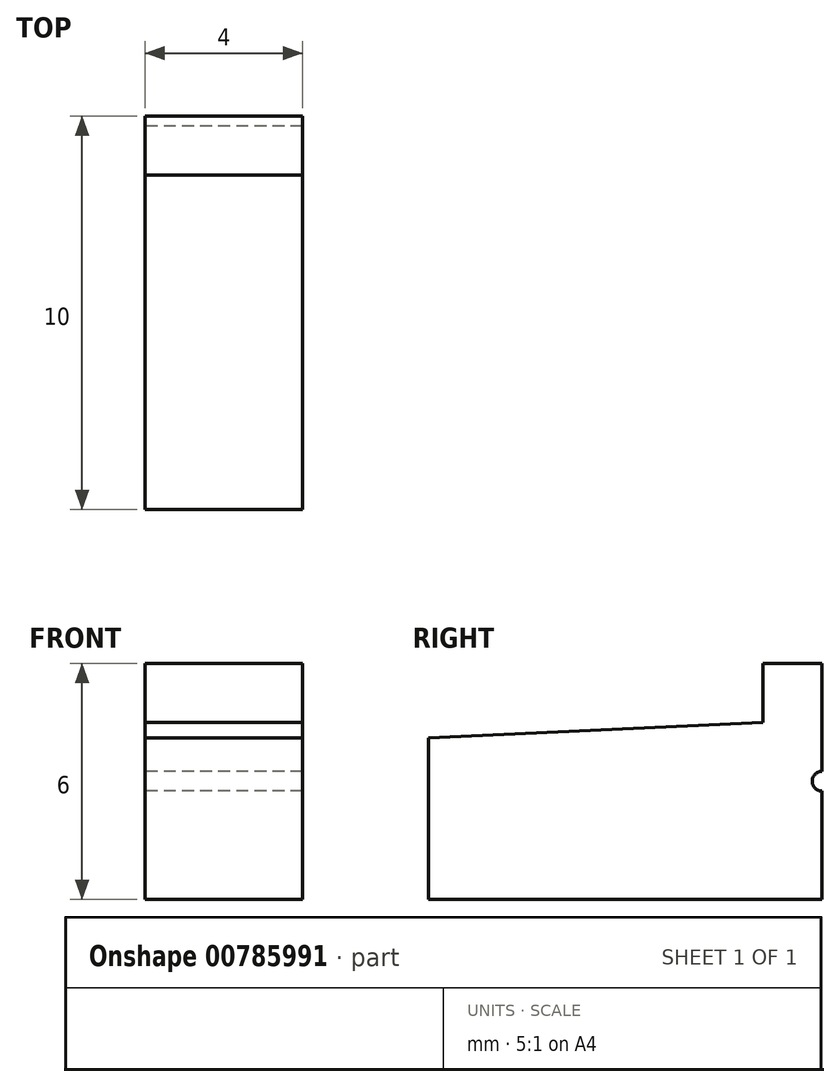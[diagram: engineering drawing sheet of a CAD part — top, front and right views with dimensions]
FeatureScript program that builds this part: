
annotation { "Feature Type Name" : "Feature", "Feature Type Description" : "" }
export const myFeature = defineFeature(function(context is Context, id is Id, definition is map)
    precondition{}
    {
        {
            var Q0;
            Q0=qCreatedBy(makeId("Front.planeOp"),FACE);
            var sketch = newSketch(context, id + "F0", { "sketchPlane" : qUnion([Q0])});
            skLineSegment(sketch, "E0.bottom", {"start": v(2, -3) * mm, "end": v(-2, -3) * mm});
            skLineSegment(sketch, "E0.top", {"start": v(2, 3) * mm, "end": v(-2, 3) * mm});
            skLineSegment(sketch, "E0.left", {"start": v(2, -3) * mm, "end": v(2, 3) * mm});
            skLineSegment(sketch, "E0.right", {"start": v(-2, -3) * mm, "end": v(-2, 3) * mm});
            skPoint(sketch, "E0.middle", {"position": v(0, 0) * mm});
            skSolve(sketch);
        }
        {
            var Q0;
            Q0=qSketchRegion(id+"F0",true);
            extrude(context, id + "F1", {"entities" : qUnion([Q0]), "depth" : 10 * mm, "offsetDistance" : 25 * mm});
        }
        {
            var Q0;
            Q0=makeQuery(id+"F1.opExtrude","SWEPT_FACE",FACE,{"disambiguationData":[OSD([sQuery(id+"F0.wireOp",EDGE,"E0.right")])]});
            var sketch = newSketch(context, id + "F2", { "sketchPlane" : qUnion([Q0])});
            skSolve(sketch);
        }
        {
            var Q0;
            {var subQ0=sQuery(id+"F0.wireOp",EDGE,"E0.right");Q0=makeQuery(id+"F2.imprint","IMPRINT",FACE,{"disambiguationData":[TD([[makeQuery(id+"F2.imprint","IMPRINT",EDGE,{"derivedFrom":makeQuery(id+"F1.opExtrude","CAP_EDGE",EDGE,{"disambiguationData":[OSD([subQ0])],"isStart":true})}),-1.0]])]});}
            var sketch = newSketch(context, id + "F3", { "sketchPlane" : qUnion([Q0])});
            skLineSegment(sketch, "E1", {"start": v(1.5, 1.5) * mm, "end": v(10, 1.1) * mm});
            skLineSegment(sketch, "E2.bottom", {"start": v(0, -3) * mm, "end": v(10, -3) * mm});
            skLineSegment(sketch, "E2.top", {"start": v(0, 3) * mm, "end": v(10, 3) * mm});
            skLineSegment(sketch, "E2.left", {"start": v(0, -3) * mm, "end": v(0, 3) * mm});
            skLineSegment(sketch, "E2.right", {"start": v(10, -3) * mm, "end": v(10, 3) * mm});
            skCircle(sketch, "E3", {"center": v(0, 0) * mm, "radius": 0.25 * mm});
            skLineSegment(sketch, "E4", {"start": v(1.5, 3) * mm, "end": v(1.5, -3) * mm});
            skPoint(sketch, "E4.endSnap0", {"position": v(5, -3) * mm});
            skSolve(sketch);
        }
        {
            var Q0;
            {var subQ0=sQuery(id+"F3.wireOp",EDGE,"E1");Q0=makeQuery(id+"F3.imprint","IMPRINT",FACE,{"disambiguationData":[TD([[makeQuery(id+"F3.imprint","IMPRINT",EDGE,{"derivedFrom":subQ0}),1.0]])]});}
            var Q1;
            {var subQ0=sQuery(id+"F3.wireOp",EDGE,"E3");var subQ1=sQuery(id+"F3.wireOp",EDGE,"E2.left");var subQ2=makeQuery(id+"F3.imprint","INTERSECT",VERTEX,{"disambiguationData":[OD(0.0)],"derivedFrom":[subQ1,subQ0]});Q1=makeQuery(id+"F3.imprint","IMPRINT",FACE,{"disambiguationData":[TD([[makeQuery(id+"F3.imprint","IMPRINT",EDGE,{"disambiguationData":[TD([[subQ2,-1.0]])],"derivedFrom":subQ1}),-1.0]])]});}
            extrude(context, id + "F4", {"entities" : qUnion([Q0, Q1]), "operationType" : NewBodyOperationType.REMOVE, "oppositeDirection" : true, "depth" : 25 * mm, "offsetDistance" : 25 * mm});
        }
    });
